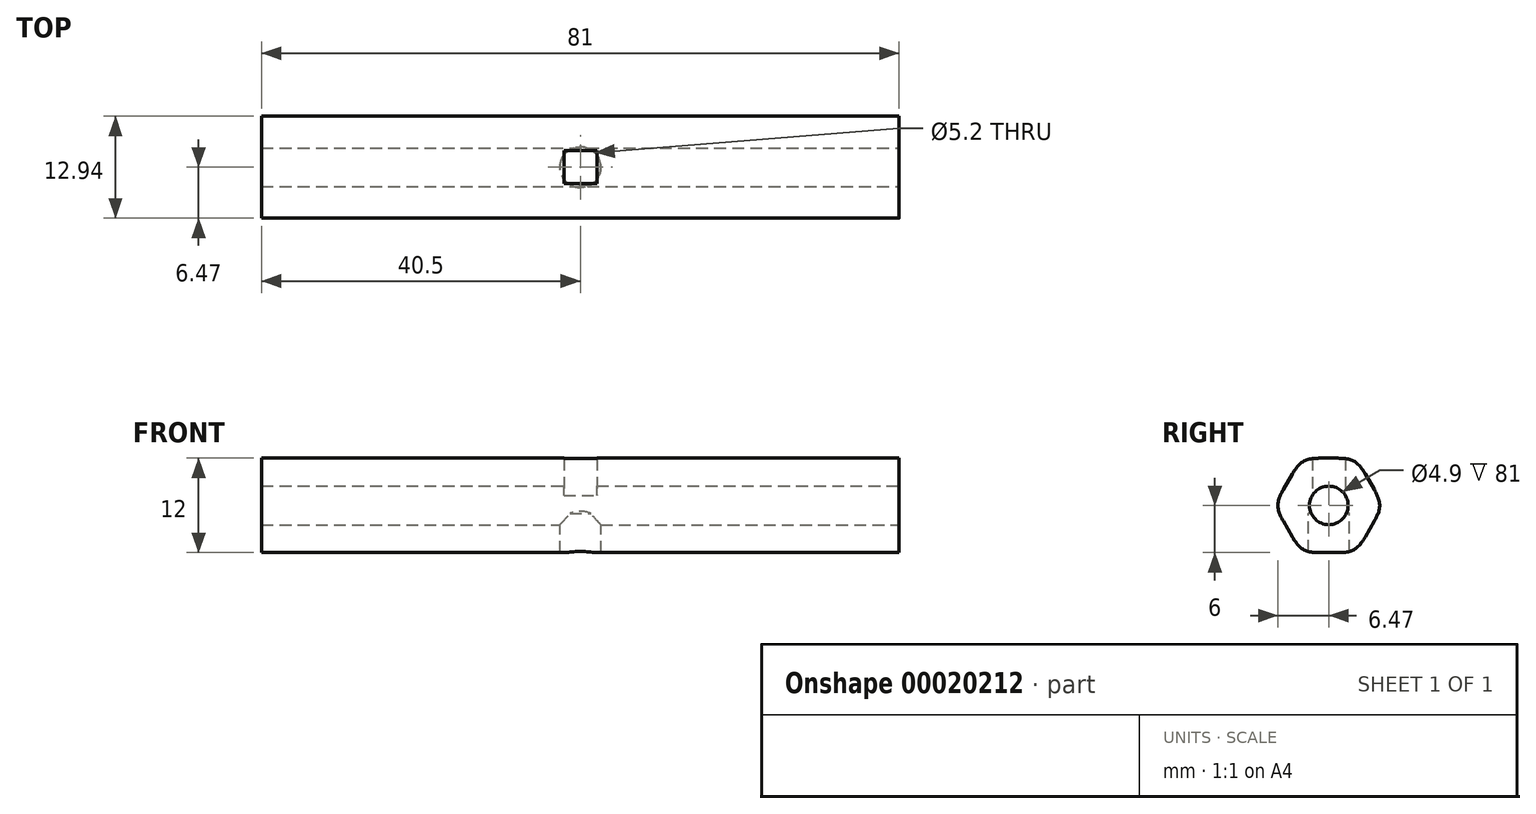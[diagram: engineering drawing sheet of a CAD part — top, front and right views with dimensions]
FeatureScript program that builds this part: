
annotation { "Feature Type Name" : "Feature", "Feature Type Description" : "" }
export const myFeature = defineFeature(function(context is Context, id is Id, definition is map)
    precondition{}
    {
        {
            var Q0;
            Q0=qCreatedBy(makeId("Right.planeOp"),FACE);
            var sketch = newSketch(context, id + "F0", { "sketchPlane" : qUnion([Q0])});
            skCircle(sketch, "E0", {"center": v(0, 0) * mm, "radius": 6 * mm, "construction": true});
            skLineSegment(sketch, "E1", {"start": v(-3.46, 6) * mm, "end": v(3.46, 6) * mm});
            skLineSegment(sketch, "E2", {"start": v(3.46, 6) * mm, "end": v(6.93, 0) * mm});
            skLineSegment(sketch, "E3", {"start": v(6.93, 0) * mm, "end": v(3.46, -6) * mm});
            skLineSegment(sketch, "E4", {"start": v(3.46, -6) * mm, "end": v(-3.46, -6) * mm});
            skLineSegment(sketch, "E5", {"start": v(-3.46, -6) * mm, "end": v(-6.93, 0) * mm});
            skLineSegment(sketch, "E6", {"start": v(-6.93, 0) * mm, "end": v(-3.46, 6) * mm});
            skSolve(sketch);
        }
        {
            var Q0;
            Q0=makeQuery(id+"F0.imprint","IMPRINT",FACE,{"disambiguationData":[TD([[makeQuery(id+"F0.imprint","IMPRINT",EDGE,{"derivedFrom":sQuery(id+"F0.wireOp",EDGE,"E1")}),-1.0]])]});
            extrude(context, id + "F1", {"entities" : qUnion([Q0]), "endBound" : BoundingType.SYMMETRIC, "depth" : 81 * mm});
        }
        {
            var Q0;
            Q0=makeQuery(id+"F1.opExtrude","CAP_FACE",FACE,{"disambiguationData":[OSD([sQuery(id+"F0.wireOp",EDGE,"E1"),sQuery(id+"F0.wireOp",EDGE,"E2"),sQuery(id+"F0.wireOp",EDGE,"E3"),sQuery(id+"F0.wireOp",EDGE,"E4"),sQuery(id+"F0.wireOp",EDGE,"E5"),sQuery(id+"F0.wireOp",EDGE,"E6")])],"isStart":false});
            var sketch = newSketch(context, id + "F2", { "sketchPlane" : qUnion([Q0])});
            skCircle(sketch, "E7", {"center": v(0, 0) * mm, "radius": 2.45 * mm});
            skSolve(sketch);
        }
        {
            var Q0;
            Q0=qSketchRegion(id+"F2",true);
            extrude(context, id + "F3", {"entities" : qUnion([Q0]), "operationType" : NewBodyOperationType.REMOVE, "endBound" : BoundingType.THROUGH_ALL, "oppositeDirection" : true, "depth" : 25 * mm});
        }
        {
            var Q0;
            Q0=qCreatedBy(makeId("Top.planeOp"),FACE);
            var sketch = newSketch(context, id + "F4", { "sketchPlane" : qUnion([Q0])});
            skLineSegment(sketch, "E8.rect.bottom", {"start": v(-2.1, 2.1) * mm, "end": v(2.1, 2.1) * mm});
            skLineSegment(sketch, "E8.rect.top", {"start": v(-2.1, -2.1) * mm, "end": v(2.1, -2.1) * mm});
            skLineSegment(sketch, "E8.rect.left", {"start": v(-2.1, 2.1) * mm, "end": v(-2.1, -2.1) * mm});
            skLineSegment(sketch, "E8.rect.right", {"start": v(2.1, 2.1) * mm, "end": v(2.1, -2.1) * mm});
            skPoint(sketch, "E8.rect.middle", {"position": v(0, 0) * mm});
            skSolve(sketch);
        }
        {
            var Q0;
            Q0=qSketchRegion(id+"F4",true);
            var Q1;
            Q1=makeQuery(id+"F1.opExtrude","SWEPT_FACE",FACE,{"disambiguationData":[OSD([sQuery(id+"F0.wireOp",EDGE,"E1")])]});
            extrude(context, id + "F5", {"entities" : qUnion([Q0]), "operationType" : NewBodyOperationType.REMOVE, "endBound" : BoundingType.THROUGH_ALL, "endBoundEntityFace" : qUnion([Q1]), "depth" : 12 * mm});
        }
        {
            var Q0;
            Q0=makeQuery(id+"F1.opExtrude","SWEPT_EDGE",EDGE,{"disambiguationData":[OSD([sQuery(id+"F0.wireOp",EDGE,"E1"),sQuery(id+"F0.wireOp",EDGE,"E6")])]});
            var Q1;
            Q1=makeQuery(id+"F1.opExtrude","SWEPT_EDGE",EDGE,{"disambiguationData":[OSD([sQuery(id+"F0.wireOp",EDGE,"E1"),sQuery(id+"F0.wireOp",EDGE,"E2")])]});
            var Q2;
            Q2=makeQuery(id+"F1.opExtrude","SWEPT_EDGE",EDGE,{"disambiguationData":[OSD([sQuery(id+"F0.wireOp",EDGE,"E2"),sQuery(id+"F0.wireOp",EDGE,"E3")])]});
            var Q3;
            Q3=makeQuery(id+"F1.opExtrude","SWEPT_EDGE",EDGE,{"disambiguationData":[OSD([sQuery(id+"F0.wireOp",EDGE,"E5"),sQuery(id+"F0.wireOp",EDGE,"E6")])]});
            var Q4;
            Q4=makeQuery(id+"F1.opExtrude","SWEPT_EDGE",EDGE,{"disambiguationData":[OSD([sQuery(id+"F0.wireOp",EDGE,"E3"),sQuery(id+"F0.wireOp",EDGE,"E4")])]});
            var Q5;
            Q5=makeQuery(id+"F1.opExtrude","SWEPT_EDGE",EDGE,{"disambiguationData":[OSD([sQuery(id+"F0.wireOp",EDGE,"E4"),sQuery(id+"F0.wireOp",EDGE,"E5")])]});
            fillet(context, id + "F6", {"entities" : qUnion([Q0, Q1, Q2, Q3, Q4, Q5]), "radius" : 4 * mm, "tangentPropagation" : true, "rho" : .6, "crossSection" : FilletCrossSection.CONIC, "allowEdgeOverflow" : false});
        }
        {
            var Q0;
            Q0=qCreatedBy(makeId("Top.planeOp"),FACE);
            var sketch = newSketch(context, id + "F7", { "sketchPlane" : qUnion([Q0])});
            skCircle(sketch, "E9", {"center": v(0, 0) * mm, "radius": 2.6 * mm});
            skSolve(sketch);
        }
        {
            var Q0;
            Q0 = qSketchRegion(id + "F7", true);
            extrude(context, id + "F8", {"entities" : qUnion([Q0]), "operationType" : NewBodyOperationType.REMOVE, "endBound" : BoundingType.THROUGH_ALL, "oppositeDirection" : true, "depth" : 25 * mm});
        }
        {
            var Q0;
            Q0=makeQuery(id+"F8.boolean.opBoolean","COPY",EDGE,{"disambiguationData":[OD(1.0)],"derivedFrom":makeQuery(id+"F8.opExtrude","CAP_EDGE",EDGE,{"disambiguationData":[OSD([sQuery(id+"F7.wireOp",EDGE,"E9")])],"isStart":true})});
            var Q1;
            Q1=makeQuery(id+"F8.boolean.opBoolean","COPY",EDGE,{"disambiguationData":[OD(0.0)],"derivedFrom":makeQuery(id+"F8.opExtrude","CAP_EDGE",EDGE,{"disambiguationData":[OSD([sQuery(id+"F7.wireOp",EDGE,"E9")])],"isStart":true})});
            chamfer(context, id + "F9", {"entities" : qUnion([Q0, Q1]), "width" : 1 * mm, "tangentPropagation" : true});
        }
    });
